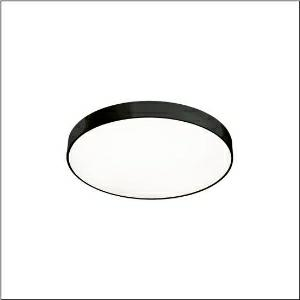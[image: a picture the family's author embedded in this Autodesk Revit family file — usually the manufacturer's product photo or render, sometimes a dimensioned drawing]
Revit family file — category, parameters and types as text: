
# Revit family: round_21_m_51mr36gm8421b
name_source: partatom
category: Lighting Fixtures
units: mm (PartAtom-declared; Revit-internal decimal feet)

## family parameters
Cut with Voids When Loaded = No
Host = Face
Light Source = No
Part Type = Normal
Room Calculation Point = No
Round Connector Dimension = Use Diameter
Shared = No

## types (1)
- --- (1 x LED, 8960 lm, 62.3 W, 4000K)
    Apparent Load = 62 VA
    CIE Flux Codes = 49 80 96 85 100
    Color Rendering = 80
    Color Temperature = 4000K
    Default Elevation = 1800 mm
    Description = Round 21 M, wall and ceiling luminaire, primary optical cover: cover, of PMMA, opal, light emission: direct/indirect distribution, primary light characteristic: symmetric, installation type: suspended mounting, surface-mounted, LED, rated luminous flux: 8.190lm, luminous efficacy: 135lm/W, light colour: 840, colour temperature: 4000K, control gear: ON/OFF Multilumen, with terminal, 3-pole, mains connection: 230V, AC, 50/60Hz, rated input power: 61W, housing, of aluminium, coated, black, diameter: 600mm, height: 62mm, protection rating (complete): IP40, insulation class (complete): insulation class I (protective earthing), certification: CE, impact resistance: IK04, permissible operating ambient temperature: -10..+35°C, packaging unit: 1 piece
    Height = 87 mm
    Lamp = 1 x LED
    Lamp Light Flux = 8960 lm
    Lamp Power = 62.3 W
    Lamp count = 1
    Length = 600 mm
    Luminous efficacy = 144 lm/W
    Manufacturer = Siteco
    ModVariant = No
    Model = 51MR36GM8421B
    Mounting Place = Ceiling
    Mounting Type = Surface mounted
    Number of Poles = 1
    OnlyDefault = Yes
    Power Factor = 1
    Product Name = Round 21 M
    Product group = wall and ceiling luminaire
    ProductGroupID = 304
    Protection Class = Protection class I
    Protection Degree = IP 40
    RLX_Detail_Level = 1
    RLX_Emergency_Light_Flux = 0 lm
    RLX_Emergency_Type = 0
    RLX_Emergency_Type_DB = No
    RlxData = <blob elided: 20849 chars, md5=25fba87a>
    Socket = socket
    Standby Power = 0 W
    System Light Flux = 8960 lm
    System Power = 62 W
    Type Comments = factory setting: luminous flux: 100 % | (ON | ON | ON | ON) | 700 mA
    Type Image = l_1258332.jpg
    URL = http://relux.com
    VarID = @adj_032686
    Voltage = 0 V
    Weight = 0.00 kg
    Width = 0 mm  [stored 0 ft]

note: [stored X ft] marks values corroborated as IEEE doubles in the binary element streams (Revit-internal decimal feet)

## geometry (parser evidence)
native form markers: Blend x4, Sweep x12
no freeform markers — native parametric forms only
